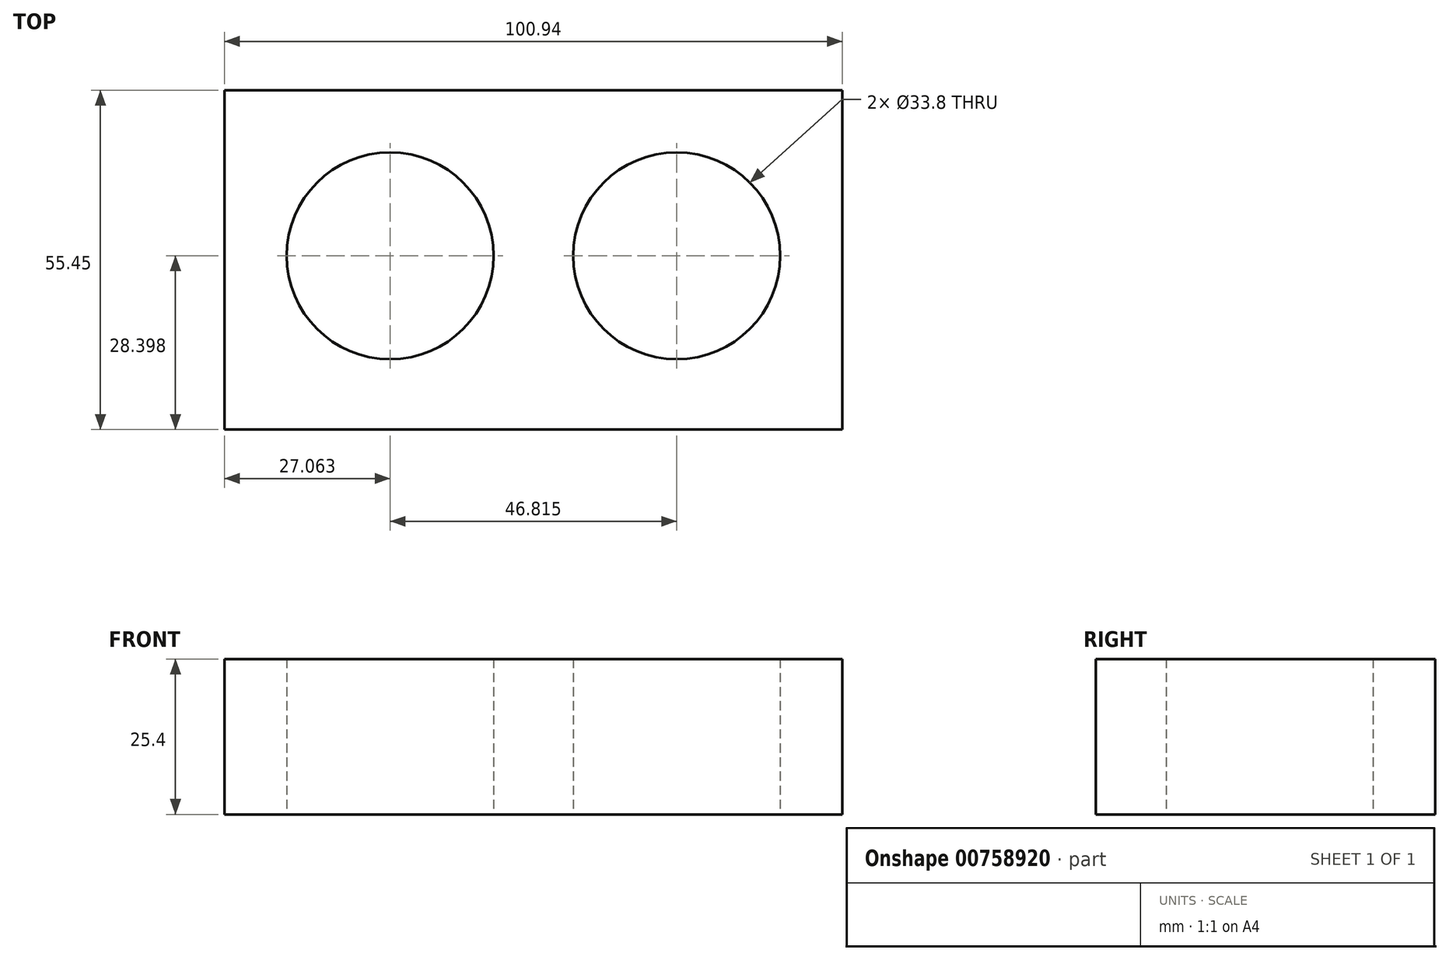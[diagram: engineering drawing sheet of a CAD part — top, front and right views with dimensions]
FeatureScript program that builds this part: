
annotation { "Feature Type Name" : "Feature", "Feature Type Description" : "" }
export const myFeature = defineFeature(function(context is Context, id is Id, definition is map)
    precondition{}
    {
        {
            var Q0;
            Q0=qCreatedBy(makeId("Top.planeOp"),FACE);
            var sketch = newSketch(context, id + "F0", { "sketchPlane" : qUnion([Q0])});
            skLineSegment(sketch, "E0.bottom", {"start": v(-55.19, 61.3) * mm, "end": v(45.75, 61.3) * mm});
            skLineSegment(sketch, "E0.top", {"start": v(-55.19, 5.86) * mm, "end": v(45.75, 5.86) * mm});
            skLineSegment(sketch, "E0.left", {"start": v(-55.19, 61.3) * mm, "end": v(-55.19, 5.86) * mm});
            skLineSegment(sketch, "E0.right", {"start": v(45.75, 61.3) * mm, "end": v(45.75, 5.86) * mm});
            skCircle(sketch, "E1", {"center": v(18.69, 34.26) * mm, "radius": 16.9 * mm});
            skPoint(sketch, "E1.first.point", {"position": v(7.44, 46.87) * mm});
            skPoint(sketch, "E1.second.point", {"position": v(24.94, 18.56) * mm});
            skPoint(sketch, "E1.third.point", {"position": v(12.43, 18.56) * mm});
            skCircle(sketch, "E2", {"center": v(-28.13, 34.26) * mm, "radius": 16.9 * mm});
            skPoint(sketch, "E2.first.point", {"position": v(-39.37, 46.87) * mm});
            skPoint(sketch, "E2.second.point", {"position": v(-21.87, 18.56) * mm});
            skPoint(sketch, "E2.third.point", {"position": v(-34.38, 18.56) * mm});
            skSolve(sketch);
        }
        {
            var Q0;
            Q0=makeQuery(id+"F0.imprint","IMPRINT",FACE,{"disambiguationData":[TD([[makeQuery(id+"F0.imprint","IMPRINT",EDGE,{"derivedFrom":sQuery(id+"F0.wireOp",EDGE,"E0.bottom")}),-1.0]])]});
            extrude(context, id + "F1", {"entities" : qUnion([Q0]), "depth" : 25.4 * mm, "offsetDistance" : 25.4 * mm});
        }
    });
